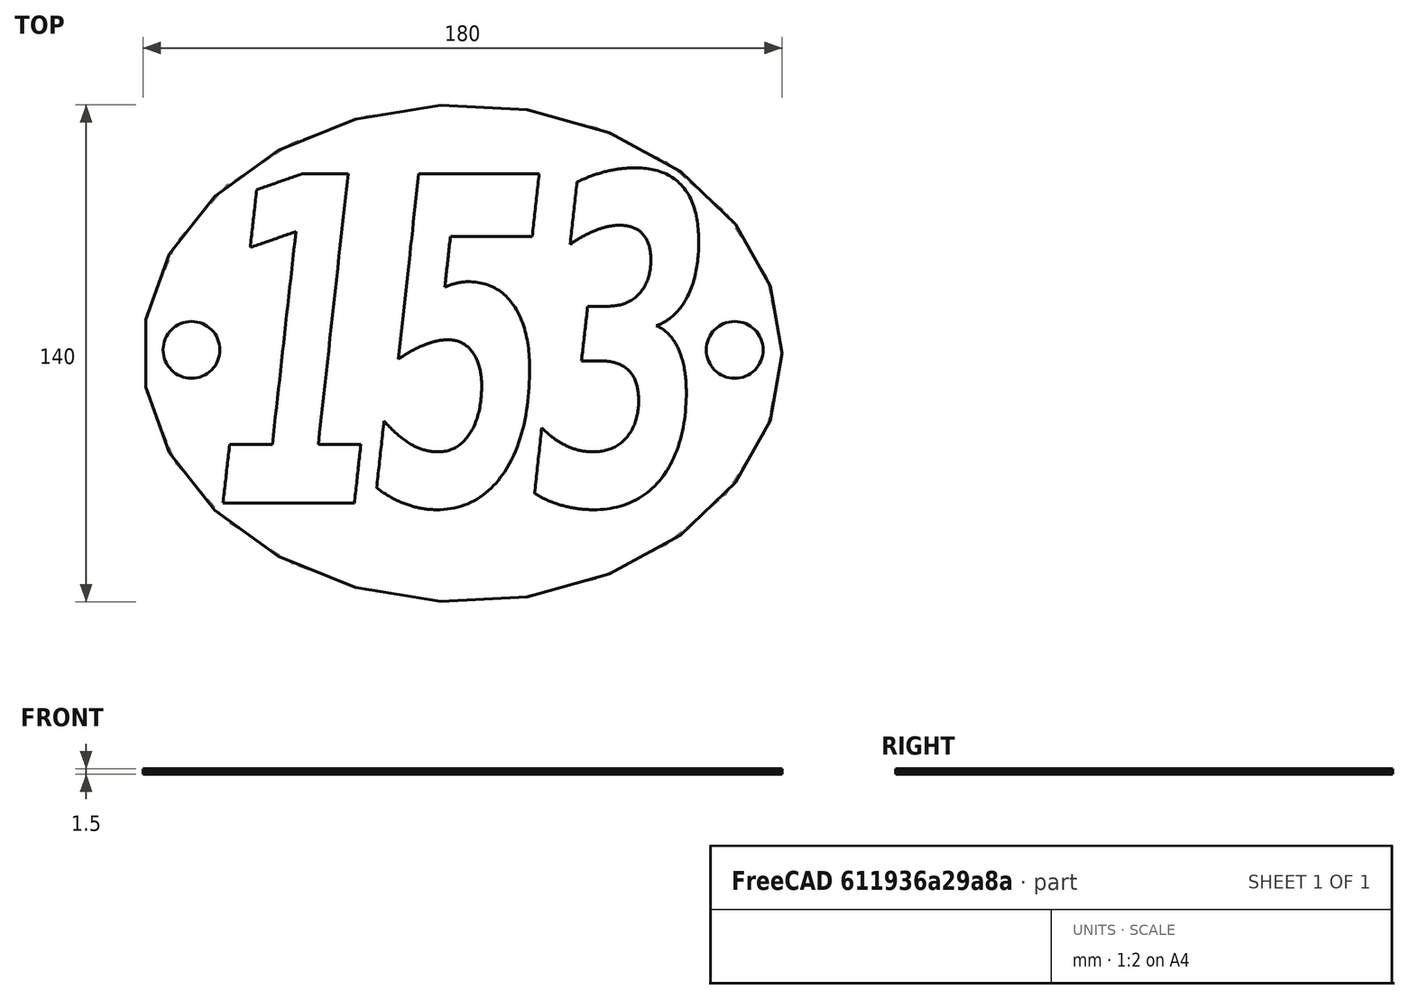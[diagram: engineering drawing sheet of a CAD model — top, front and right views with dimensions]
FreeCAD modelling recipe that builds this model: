
FCSTD DOCUMENT  (FreeCAD 0.18.4R)
Label: placa_solo_numero
License: All rights reserved
LicenseURL: http://en.wikipedia.org/wiki/All_rights_reserved
objects: Part::Cut×11, Part::Extrusion×8, Part::Feature×6, Part::FeaturePython×6, Part::Cylinder×4, Part::Part2DObjectPython×2, Part::Box×1
note: 38 computed .brp shape members not serialized (recipe doc carries the construction recipe); baked Part::Feature solids carry a one-line shape summary decoded from their .brp

FEATURE [Part::Part2DObjectPython] Ellipse  # Draft 2D object (typed FeaturePython)
  FirstAngle = 0
  LastAngle = 0
  MajorRadius = 90
  MakeFace = true
  MinorRadius = 70
  Placement = pos=(60.32,-53.96,0) rot=(0,0,1;0rad)
FEATURE [Part::Extrusion] Extrude017  label="elipse"
  Base = -> Ellipse
  Dir = (0,0,1)
  DirMode = 2
  FaceMakerClass = Part::FaceMakerBullseye
  LengthFwd = 1.5
  LengthRev = 0
  Placement = pos=(6,0,-16) rot=(0,0,1;0rad)
  Solid = true
  Symmetric = false
FEATURE [Part::Feature] path819
  shape: bbox 32.35 x 77.3 x 2.649e-07 mm, 0 faces, 0 solids (baked)
FEATURE [Part::Extrusion] Extrude_path819  label="1_janaya"
  Base = -> path819
  Dir = (0,0,10)
  DirMode = 0
  FaceMakerClass = Part::FaceMakerExtrusion
  LengthFwd = 0
  LengthRev = 0
  Placement = pos=(0,0,-20) rot=(0,0,1;0rad)
  Solid = true
  Symmetric = false
FEATURE [Part::Feature] path823
  shape: bbox 38.52 x 80.2 x 2.649e-07 mm, 0 faces, 0 solids (baked)
FEATURE [Part::Extrusion] Extrude_path823  label="3_janaya"
  Base = -> path823
  Dir = (0,0,10)
  DirMode = 0
  FaceMakerClass = Part::FaceMakerExtrusion
  LengthFwd = 0
  LengthRev = 0
  Placement = pos=(0,0,-20) rot=(0,0,1;0rad)
  Solid = true
  Symmetric = false
FEATURE [Part::Feature] path821
  shape: bbox 38.14 x 78.8 x 2.649e-07 mm, 0 faces, 0 solids (baked)
FEATURE [Part::Extrusion] Extrude_path821  label="5_janaya"
  Base = -> path821
  Dir = (0,0,10)
  DirMode = 0
  FaceMakerClass = Part::FaceMakerExtrusion
  LengthFwd = 0
  LengthRev = 0
  Placement = pos=(0,0,-20) rot=(0,0,1;0rad)
  Solid = true
  Symmetric = false
FEATURE [Part::FeaturePython] Clone  label="1_jan  ya001"  # Draft clone (typed FeaturePython)
  AttacherType = Attacher::AttachEngine3D
  Fuse = false
  Objects = -> [Extrude_path819]
  Placement = pos=(-6,1,-20) rot=(0,0,1;0rad)
  Scale = (1.2,1.2,1.2)
FEATURE [Part::FeaturePython] Clone001  label="5_jan  ya001"  # Draft clone (typed FeaturePython)
  AttacherType = Attacher::AttachEngine3D
  Fuse = false
  Objects = -> [Extrude_path821]
  Placement = pos=(-11,1,-20) rot=(0,0,1;0rad)
  Scale = (1.2,1.2,1.2)
FEATURE [Part::FeaturePython] Clone002  label="3_jan  ya001"  # Draft clone (typed FeaturePython)
  AttacherType = Attacher::AttachEngine3D
  Fuse = false
  Objects = -> [Extrude_path823]
  Placement = pos=(-16,1,-20) rot=(0,0,1;0rad)
  Scale = (1.2,1.2,1.2)
FEATURE [Part::Cut] Cut
  Base = -> Extrude017
  Tool = -> Clone
FEATURE [Part::Cut] Cut001
  Base = -> Cut
  Tool = -> Clone001
FEATURE [Part::Cut] Cut002
  Base = -> Cut001
  Tool = -> Clone002
FEATURE [Part::Cylinder] Cylinder
  Angle = 360
  AttacherType = Attacher::AttachEngine3D
  Height = 10
  Placement = pos=(-10,-53,-20) rot=(0,0,1;0rad)
  Radius = 8
FEATURE [Part::Cylinder] Cylinder001
  Angle = 360
  AttacherType = Attacher::AttachEngine3D
  Height = 10
  Placement = pos=(143,-53,-20) rot=(0,0,1;0rad)
  Radius = 8
FEATURE [Part::Cut] Cut003
  Base = -> Cut002
  Tool = -> Cylinder
FEATURE [Part::Cut] Cut004  label="placa_solo_numero_15"
  Base = -> Cut003
  Tool = -> Cylinder001
FEATURE [Part::Box] Box  label="Cube"
  AttacherType = Attacher::AttachEngine3D
  Height = 10
  Length = 250
  Placement = pos=(-52,-135,-15.2) rot=(0,0,1;0rad)
  Width = 250
FEATURE [Part::Feature] path824
  shape: bbox 32.35 x 77.3 x 2.649e-07 mm, 0 faces, 0 solids (baked)
FEATURE [Part::Extrusion] Extrude_path824  label="1_janaya001"
  Base = -> path824
  Dir = (0,0,10)
  DirMode = 0
  FaceMakerClass = Part::FaceMakerExtrusion
  LengthFwd = 0
  LengthRev = 0
  Placement = pos=(0,0,-20) rot=(0,0,1;0rad)
  Solid = true
  Symmetric = false
FEATURE [Part::FeaturePython] Clone004  label="1_jan  ya002"  # Draft clone (typed FeaturePython)
  AttacherType = Attacher::AttachEngine3D
  Fuse = false
  Objects = -> [Extrude_path824]
  Placement = pos=(-6,1,-20) rot=(0,0,1;0rad)
  Scale = (1.2,1.2,1.2)
FEATURE [Part::Feature] path825
  shape: bbox 38.14 x 78.8 x 2.649e-07 mm, 0 faces, 0 solids (baked)
FEATURE [Part::Extrusion] Extrude_path825  label="5_janaya001"
  Base = -> path825
  Dir = (0,0,10)
  DirMode = 0
  FaceMakerClass = Part::FaceMakerExtrusion
  LengthFwd = 0
  LengthRev = 0
  Placement = pos=(0,0,-20) rot=(0,0,1;0rad)
  Solid = true
  Symmetric = false
FEATURE [Part::FeaturePython] Clone005  label="5_jan  ya002"  # Draft clone (typed FeaturePython)
  AttacherType = Attacher::AttachEngine3D
  Fuse = false
  Objects = -> [Extrude_path825]
  Placement = pos=(-11,1,-20) rot=(0,0,1;0rad)
  Scale = (1.2,1.2,1.2)
FEATURE [Part::Part2DObjectPython] Ellipse001  # Draft 2D object (typed FeaturePython)
  FirstAngle = 0
  LastAngle = 0
  MajorRadius = 90
  MakeFace = true
  MinorRadius = 70
  Placement = pos=(60.32,-53.96,0) rot=(0,0,1;0rad)
FEATURE [Part::Extrusion] Extrude018  label="elipse001"
  Base = -> Ellipse001
  Dir = (0,0,1)
  DirMode = 2
  FaceMakerClass = Part::FaceMakerBullseye
  LengthFwd = 1.5
  LengthRev = 0
  Placement = pos=(6,0,-16) rot=(0,0,1;0rad)
  Solid = true
  Symmetric = false
FEATURE [Part::Feature] path826
  shape: bbox 38.52 x 80.2 x 2.649e-07 mm, 0 faces, 0 solids (baked)
FEATURE [Part::Extrusion] Extrude_path826  label="3_janaya001"
  Base = -> path826
  Dir = (0,0,10)
  DirMode = 0
  FaceMakerClass = Part::FaceMakerExtrusion
  LengthFwd = 0
  LengthRev = 0
  Placement = pos=(0,0,-20) rot=(0,0,1;0rad)
  Solid = true
  Symmetric = false
FEATURE [Part::FeaturePython] Clone003  label="3_jan  ya002"  # Draft clone (typed FeaturePython)
  AttacherType = Attacher::AttachEngine3D
  Fuse = false
  Objects = -> [Extrude_path826]
  Placement = pos=(-16,1,-20) rot=(0,0,1;0rad)
  Scale = (1.2,1.2,1.2)
FEATURE [Part::Cut] Cut006
  Base = -> Extrude018
  Tool = -> Clone004
FEATURE [Part::Cut] Cut008
  Base = -> Cut006
  Tool = -> Clone005
FEATURE [Part::Cut] Cut005
  Base = -> Cut008
  Tool = -> Clone003
FEATURE [Part::Cylinder] Cylinder002
  Angle = 360
  AttacherType = Attacher::AttachEngine3D
  Height = 10
  Placement = pos=(143,-53,-20) rot=(0,0,1;0rad)
  Radius = 8
FEATURE [Part::Cylinder] Cylinder003
  Angle = 360
  AttacherType = Attacher::AttachEngine3D
  Height = 10
  Placement = pos=(-10,-53,-20) rot=(0,0,1;0rad)
  Radius = 8
FEATURE [Part::Cut] Cut007
  Base = -> Cut005
  Tool = -> Cylinder003
FEATURE [Part::Cut] Cut009  label="placa_solo_numero_016"
  Base = -> Cut007
  Tool = -> Cylinder002
FEATURE [Part::Cut] Cut010  label="placa_solo_numero_08"
  Base = -> Cut009
  Tool = -> Box
